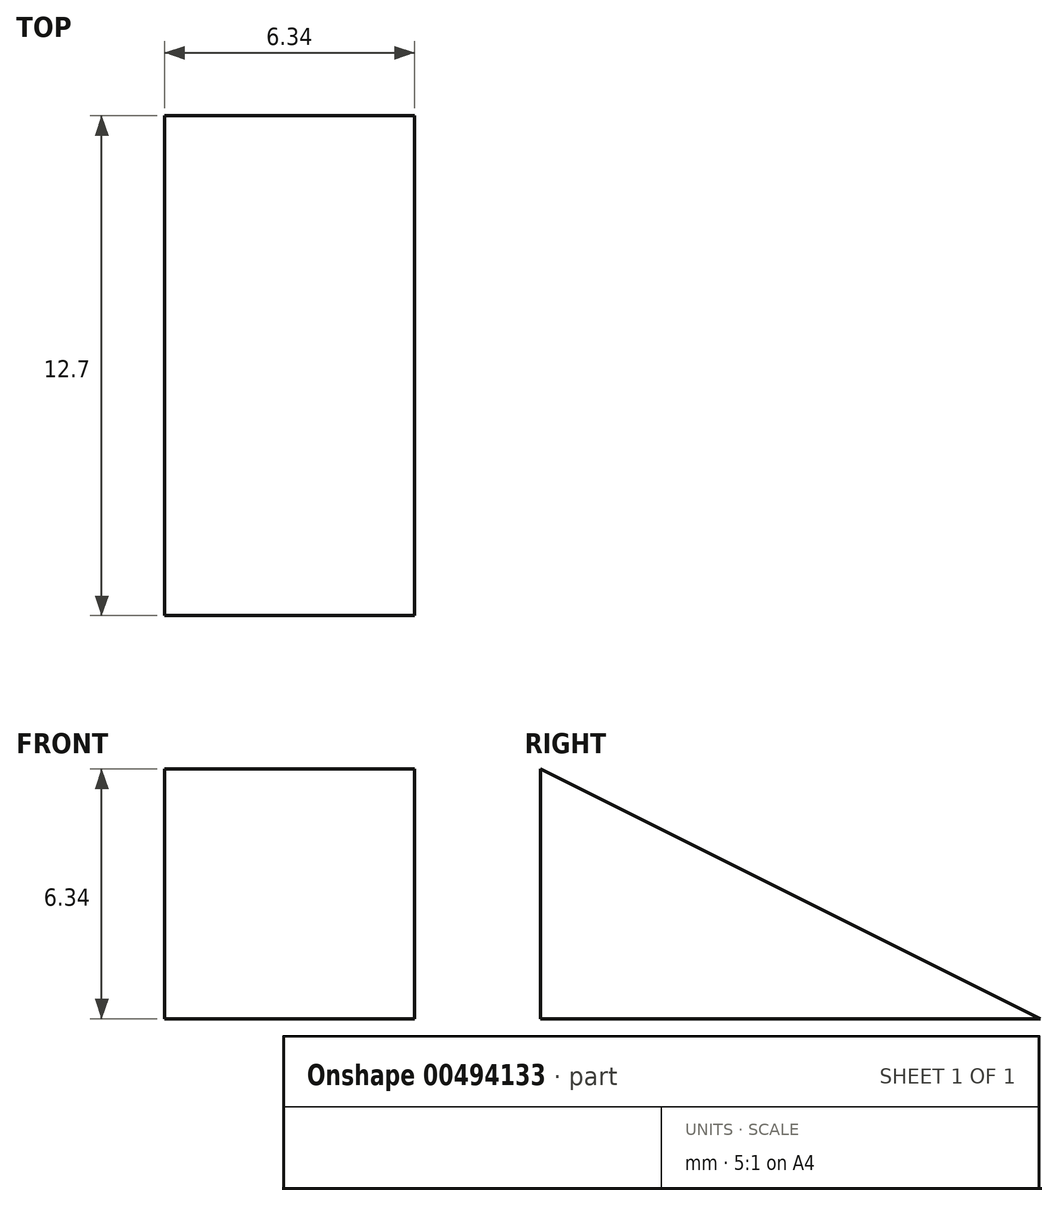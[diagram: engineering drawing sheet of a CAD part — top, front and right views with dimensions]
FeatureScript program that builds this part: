
annotation { "Feature Type Name" : "Feature", "Feature Type Description" : "" }
export const myFeature = defineFeature(function(context is Context, id is Id, definition is map)
    precondition{}
    {
        {
            var Q0;
            Q0=qCreatedBy(makeId("Right.planeOp"),FACE);
            var sketch = newSketch(context, id + "F0", { "sketchPlane" : qUnion([Q0])});
            skLineSegment(sketch, "E0.top", {"start": v(-6.35, -3.18) * mm, "end": v(6.35, -3.18) * mm});
            skLineSegment(sketch, "E0.left", {"start": v(-6.35, 3.18) * mm, "end": v(-6.35, -3.18) * mm});
            skPoint(sketch, "E0.middle", {"position": v(0, 0) * mm});
            skLineSegment(sketch, "E1", {"start": v(-6.35, 3.18) * mm, "end": v(6.35, -3.18) * mm});
            skSolve(sketch);
        }
        {
            var Q0;
            Q0 = qSketchRegion(id + "F0", true);
            extrude(context, id + "F1", {"entities" : qUnion([Q0]), "endBound" : BoundingType.SYMMETRIC, "depth" : 6.35 * mm});
        }
        {
            var Q0;
            Q0=makeQuery(id+"F1.opExtrude","SWEPT_FACE",FACE,{"disambiguationData":[OSD([sQuery(id+"F0.wireOp",EDGE,"E0.top")])]});
            var sketch = newSketch(context, id + "F2", { "sketchPlane" : qUnion([Q0])});
            skLineSegment(sketch, "E2", {"start": v(3.18, 0) * mm, "end": v(-3.18, 0) * mm});
            skSolve(sketch);
        }
    });
